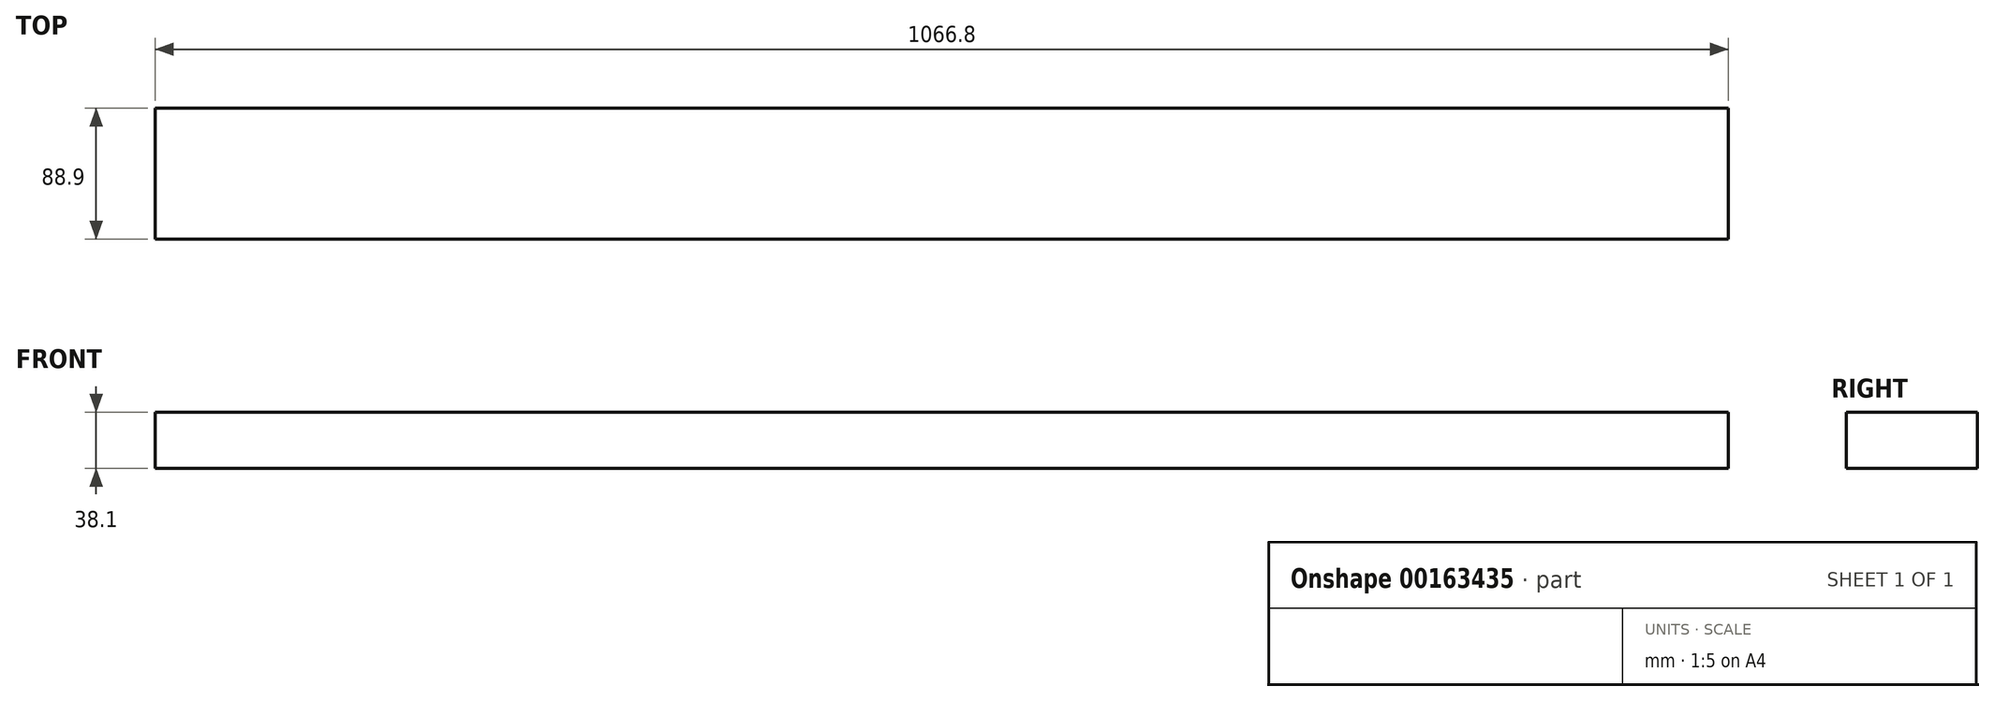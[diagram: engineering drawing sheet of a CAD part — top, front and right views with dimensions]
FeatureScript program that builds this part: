
annotation { "Feature Type Name" : "Feature", "Feature Type Description" : "" }
export const myFeature = defineFeature(function(context is Context, id is Id, definition is map)
    precondition{}
    {
        {
            var Q0;
            Q0=qCreatedBy(makeId("Right.planeOp"),FACE);
            var sketch = newSketch(context, id + "F0", { "sketchPlane" : qUnion([Q0])});
            skLineSegment(sketch, "E0.bottom", {"start": v(0, 0) * mm, "end": v(88.9, 0) * mm});
            skLineSegment(sketch, "E0.top", {"start": v(0, 38.1) * mm, "end": v(88.9, 38.1) * mm});
            skLineSegment(sketch, "E0.left", {"start": v(0, 0) * mm, "end": v(0, 38.1) * mm});
            skLineSegment(sketch, "E0.right", {"start": v(88.9, 0) * mm, "end": v(88.9, 38.1) * mm});
            skSolve(sketch);
        }
        {
            var Q0;
            Q0 = qSketchRegion(id + "F0", true);
            extrude(context, id + "F1", {"entities" : qUnion([Q0]), "depth" : 1066.8 * mm});
        }
    });
